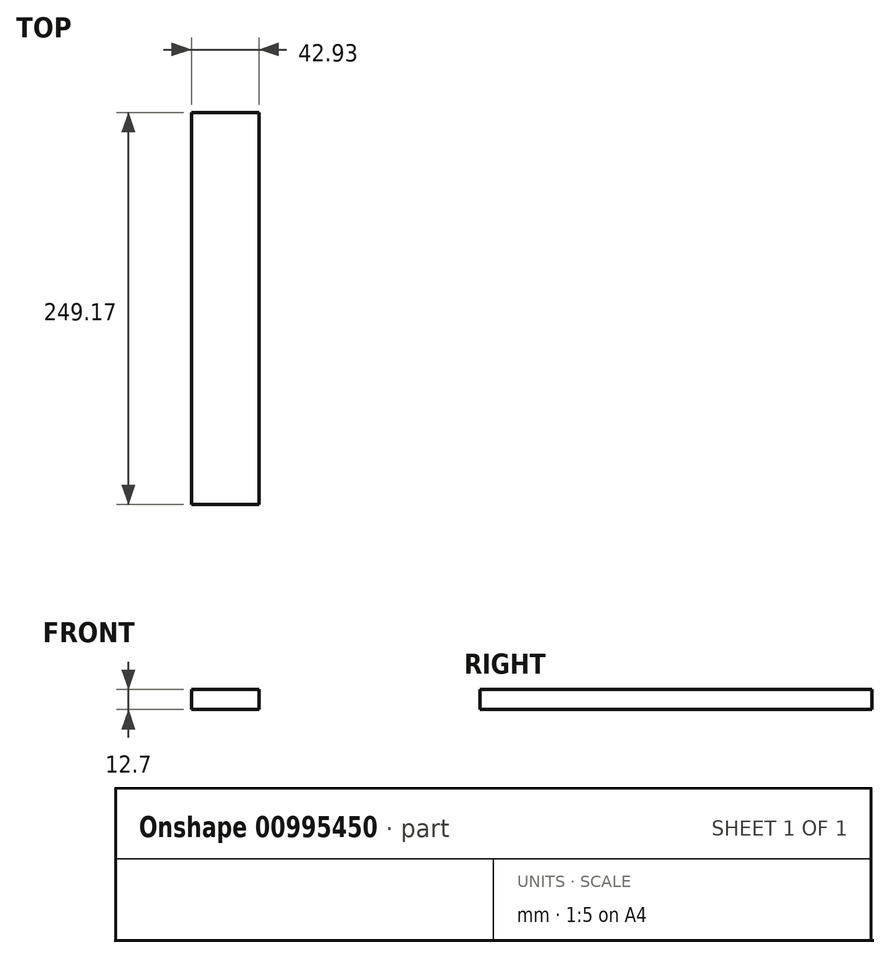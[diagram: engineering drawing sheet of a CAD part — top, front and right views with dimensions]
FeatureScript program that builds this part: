
annotation { "Feature Type Name" : "Feature", "Feature Type Description" : "" }
export const myFeature = defineFeature(function(context is Context, id is Id, definition is map)
    precondition{}
    {
        {
            var Q0;
            Q0=qCreatedBy(makeId("Front.planeOp"),FACE);
            var sketch = newSketch(context, id + "F0", { "sketchPlane" : qUnion([Q0])});
            skLineSegment(sketch, "E0.bottom", {"start": v(0, 0) * mm, "end": v(42.93, 0) * mm});
            skLineSegment(sketch, "E0.top", {"start": v(0, 12.7) * mm, "end": v(42.93, 12.7) * mm});
            skLineSegment(sketch, "E0.left", {"start": v(0, 0) * mm, "end": v(0, 12.7) * mm});
            skLineSegment(sketch, "E0.right", {"start": v(42.93, 0) * mm, "end": v(42.93, 12.7) * mm});
            skSolve(sketch);
        }
        {
            var Q0;
            Q0 = qSketchRegion(id + "F0", true);
            extrude(context, id + "F1", {"entities" : qUnion([Q0]), "oppositeDirection" : true, "depth" : 249.17 * mm, "offsetDistance" : 25.4 * mm});
        }
    });
